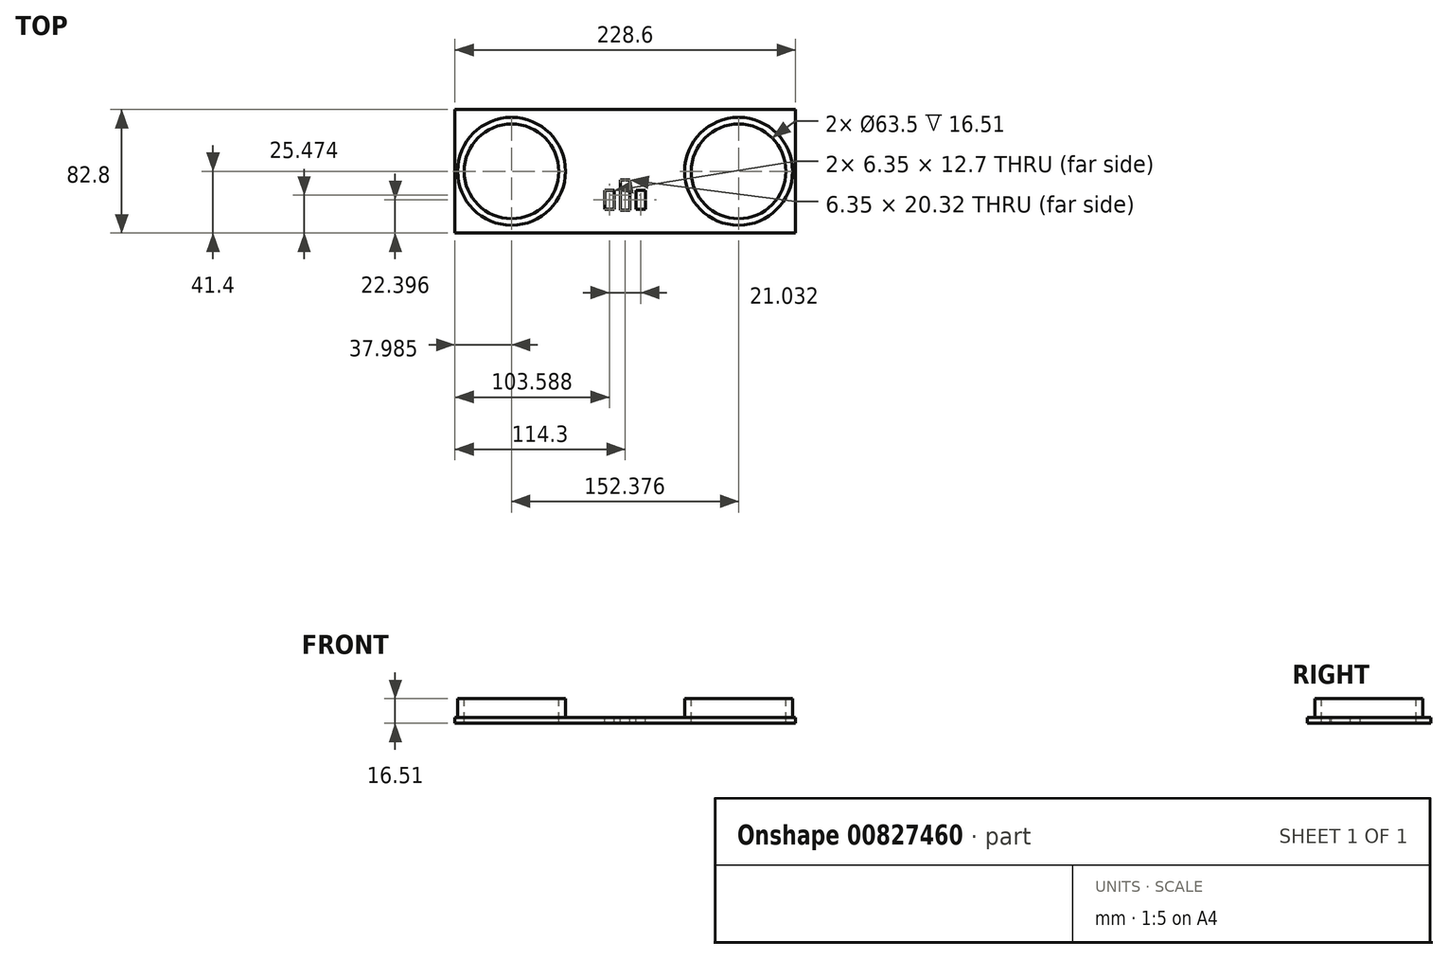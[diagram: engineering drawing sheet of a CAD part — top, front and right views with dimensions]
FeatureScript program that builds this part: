
annotation { "Feature Type Name" : "Feature", "Feature Type Description" : "" }
export const myFeature = defineFeature(function(context is Context, id is Id, definition is map)
    precondition{}
    {
        {
            var Q0;
            Q0=qCreatedBy(makeId("Top.planeOp"),FACE);
            var sketch = newSketch(context, id + "F0", { "sketchPlane" : qUnion([Q0])});
            skLineSegment(sketch, "E0.bottom", {"start": v(114.3, -41.4) * mm, "end": v(-114.3, -41.4) * mm});
            skLineSegment(sketch, "E0.top", {"start": v(114.3, 41.4) * mm, "end": v(-114.3, 41.4) * mm});
            skLineSegment(sketch, "E0.left", {"start": v(114.3, -41.4) * mm, "end": v(114.3, 41.4) * mm});
            skLineSegment(sketch, "E0.right", {"start": v(-114.3, -41.4) * mm, "end": v(-114.3, 41.4) * mm});
            skPoint(sketch, "E0.middle", {"position": v(0, 0) * mm});
            skSolve(sketch);
        }
        {
            var Q0;
            Q0 = qSketchRegion(id + "F0", true);
            extrude(context, id + "F1", {"entities" : qUnion([Q0]), "depth" : 3.8 * mm, "offsetDistance" : 25.4 * mm});
        }
        {
            var Q0;
            Q0=makeQuery(id+"F1.opExtrude","CAP_FACE",FACE,{"disambiguationData":[OSD([sQuery(id+"F0.wireOp",EDGE,"E0.bottom"),sQuery(id+"F0.wireOp",EDGE,"E0.top"),sQuery(id+"F0.wireOp",EDGE,"E0.left"),sQuery(id+"F0.wireOp",EDGE,"E0.right")])],"isStart":false});
            var sketch = newSketch(context, id + "F2", { "sketchPlane" : qUnion([Q0])});
            skCircle(sketch, "E1", {"center": v(-76.32, 0) * mm, "radius": 36.2 * mm});
            skSolve(sketch);
        }
        {
            var Q0;
            Q0 = qSketchRegion(id + "F2", true);
            extrude(context, id + "F3", {"entities" : qUnion([Q0]), "operationType" : NewBodyOperationType.ADD, "depth" : 12.7 * mm, "offsetDistance" : 25.4 * mm});
        }
        {
            var Q0;
            Q0=makeQuery(id+"F1.opExtrude","CAP_FACE",FACE,{"disambiguationData":[OSD([sQuery(id+"F0.wireOp",EDGE,"E0.bottom"),sQuery(id+"F0.wireOp",EDGE,"E0.top"),sQuery(id+"F0.wireOp",EDGE,"E0.left"),sQuery(id+"F0.wireOp",EDGE,"E0.right")])],"isStart":false});
            var sketch = newSketch(context, id + "F4", { "sketchPlane" : qUnion([Q0])});
            skCircle(sketch, "E2", {"center": v(76.06, 0) * mm, "radius": 36.2 * mm});
            skSolve(sketch);
        }
        {
            var Q0;
            Q0 = qSketchRegion(id + "F4", true);
            extrude(context, id + "F5", {"entities" : qUnion([Q0]), "operationType" : NewBodyOperationType.ADD, "depth" : 12.7 * mm, "offsetDistance" : 25.4 * mm});
        }
        {
            var Q0;
            Q0=makeQuery(id+"F3.opExtrude","CAP_FACE",FACE,{"disambiguationData":[OSD([sQuery(id+"F2.wireOp",EDGE,"E1")])],"isStart":false});
            var sketch = newSketch(context, id + "F6", { "sketchPlane" : qUnion([Q0])});
            skCircle(sketch, "E3", {"center": v(-76.32, 0) * mm, "radius": 31.75 * mm});
            skSolve(sketch);
        }
        {
            var Q0;
            Q0 = qSketchRegion(id + "F6", true);
            extrude(context, id + "F7", {"entities" : qUnion([Q0]), "operationType" : NewBodyOperationType.REMOVE, "oppositeDirection" : true, "depth" : 17.78 * mm, "offsetDistance" : 25.4 * mm});
        }
        {
            var Q0;
            Q0=makeQuery(id+"F5.opExtrude","CAP_FACE",FACE,{"disambiguationData":[OSD([sQuery(id+"F4.wireOp",EDGE,"E2")])],"isStart":false});
            var sketch = newSketch(context, id + "F8", { "sketchPlane" : qUnion([Q0])});
            skCircle(sketch, "E4", {"center": v(76.06, 0) * mm, "radius": 31.75 * mm});
            skSolve(sketch);
        }
        {
            var Q0;
            Q0 = qSketchRegion(id + "F8", true);
            extrude(context, id + "F9", {"entities" : qUnion([Q0]), "operationType" : NewBodyOperationType.REMOVE, "oppositeDirection" : true, "depth" : 17.78 * mm, "offsetDistance" : 25.4 * mm});
        }
        {
            var Q0;
            Q0=makeQuery(id+"F1.opExtrude","CAP_FACE",FACE,{"disambiguationData":[OSD([sQuery(id+"F0.wireOp",EDGE,"E0.bottom"),sQuery(id+"F0.wireOp",EDGE,"E0.top"),sQuery(id+"F0.wireOp",EDGE,"E0.left"),sQuery(id+"F0.wireOp",EDGE,"E0.right")])],"isStart":false});
            var sketch = newSketch(context, id + "F10", { "sketchPlane" : qUnion([Q0])});
            skLineSegment(sketch, "E5.bottom", {"start": v(3.17, -26.09) * mm, "end": v(-3.18, -26.09) * mm});
            skLineSegment(sketch, "E5.top", {"start": v(3.18, -5.77) * mm, "end": v(-3.17, -5.77) * mm});
            skLineSegment(sketch, "E5.left", {"start": v(3.17, -26.09) * mm, "end": v(3.18, -5.77) * mm});
            skLineSegment(sketch, "E5.right", {"start": v(-3.18, -26.09) * mm, "end": v(-3.17, -5.77) * mm});
            skPoint(sketch, "E5.middle", {"position": v(0, -15.93) * mm});
            skSolve(sketch);
        }
        {
            var Q0;
            Q0 = qSketchRegion(id + "F10", true);
            extrude(context, id + "F11", {"entities" : qUnion([Q0]), "operationType" : NewBodyOperationType.REMOVE, "oppositeDirection" : true, "depth" : 7.62 * mm, "offsetDistance" : 25.4 * mm});
        }
        {
            var Q0;
            Q0=makeQuery(id+"F1.opExtrude","CAP_FACE",FACE,{"disambiguationData":[OSD([sQuery(id+"F0.wireOp",EDGE,"E0.bottom"),sQuery(id+"F0.wireOp",EDGE,"E0.top"),sQuery(id+"F0.wireOp",EDGE,"E0.left"),sQuery(id+"F0.wireOp",EDGE,"E0.right")])],"isStart":false});
            var sketch = newSketch(context, id + "F12", { "sketchPlane" : qUnion([Q0])});
            skLineSegment(sketch, "E6.bottom", {"start": v(-7.54, -25.35) * mm, "end": v(-13.89, -25.35) * mm});
            skLineSegment(sketch, "E6.top", {"start": v(-7.54, -12.65) * mm, "end": v(-13.89, -12.65) * mm});
            skLineSegment(sketch, "E6.left", {"start": v(-7.54, -25.35) * mm, "end": v(-7.54, -12.65) * mm});
            skLineSegment(sketch, "E6.right", {"start": v(-13.89, -25.35) * mm, "end": v(-13.89, -12.65) * mm});
            skPoint(sketch, "E6.middle", {"position": v(-10.71, -19) * mm});
            skSolve(sketch);
        }
        {
            var Q0;
            Q0 = qSketchRegion(id + "F12", true);
            extrude(context, id + "F13", {"entities" : qUnion([Q0]), "operationType" : NewBodyOperationType.REMOVE, "oppositeDirection" : true, "depth" : 7.62 * mm, "offsetDistance" : 25.4 * mm});
        }
        {
            var Q0;
            Q0=makeQuery(id+"F1.opExtrude","CAP_FACE",FACE,{"disambiguationData":[OSD([sQuery(id+"F0.wireOp",EDGE,"E0.bottom"),sQuery(id+"F0.wireOp",EDGE,"E0.top"),sQuery(id+"F0.wireOp",EDGE,"E0.left"),sQuery(id+"F0.wireOp",EDGE,"E0.right")])],"isStart":false});
            var sketch = newSketch(context, id + "F14", { "sketchPlane" : qUnion([Q0])});
            skLineSegment(sketch, "E7.bottom", {"start": v(13.5, -25.35) * mm, "end": v(7.14, -25.35) * mm});
            skLineSegment(sketch, "E7.top", {"start": v(13.5, -12.65) * mm, "end": v(7.14, -12.65) * mm});
            skLineSegment(sketch, "E7.left", {"start": v(13.5, -25.35) * mm, "end": v(13.5, -12.65) * mm});
            skLineSegment(sketch, "E7.right", {"start": v(7.14, -25.35) * mm, "end": v(7.14, -12.65) * mm});
            skPoint(sketch, "E7.middle", {"position": v(10.32, -19) * mm});
            skPoint(sketch, "E7.middle.positionSnap0", {"position": v(-7.54, -19) * mm});
            skPoint(sketch, "E7.centerSnap0", {"position": v(-7.54, -19) * mm});
            skSolve(sketch);
        }
        {
            var Q0;
            Q0 = qSketchRegion(id + "F14", true);
            extrude(context, id + "F15", {"entities" : qUnion([Q0]), "operationType" : NewBodyOperationType.REMOVE, "oppositeDirection" : true, "depth" : 7.62 * mm, "offsetDistance" : 25.4 * mm});
        }
    });
